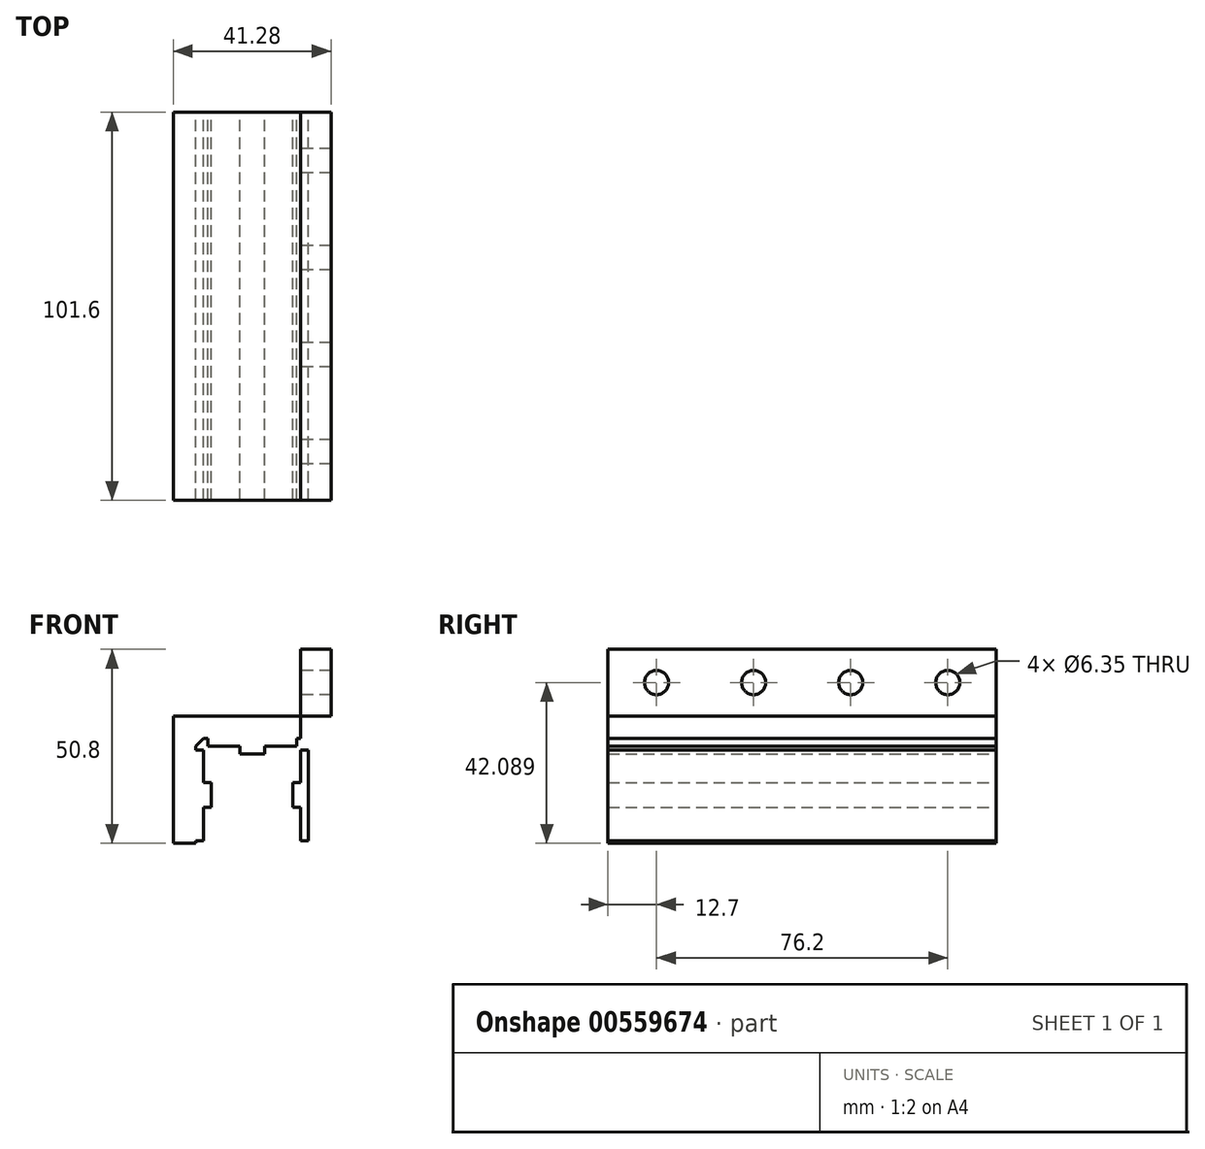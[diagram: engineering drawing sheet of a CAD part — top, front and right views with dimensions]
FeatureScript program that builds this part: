
annotation { "Feature Type Name" : "Feature", "Feature Type Description" : "" }
export const myFeature = defineFeature(function(context is Context, id is Id, definition is map)
    precondition{}
    {
        {
            var Q0;
            Q0=qCreatedBy(makeId("Front.planeOp"),FACE);
            var sketch = newSketch(context, id + "F0", { "sketchPlane" : qUnion([Q0])});
            skLineSegment(sketch, "E0.bottom", {"start": v(-20.64, 16.67) * mm, "end": v(20.64, 16.67) * mm});
            skLineSegment(sketch, "E0.top", {"start": v(-20.64, -16.67) * mm, "end": v(20.64, -16.67) * mm});
            skLineSegment(sketch, "E0.left", {"start": v(-20.64, 16.67) * mm, "end": v(-20.64, -16.67) * mm});
            skLineSegment(sketch, "E0.right", {"start": v(20.64, 16.67) * mm, "end": v(20.64, -16.67) * mm});
            skLineSegment(sketch, "E1.bottom", {"start": v(20.64, -16.67) * mm, "end": v(12.71, -16.67) * mm});
            skLineSegment(sketch, "E1.top", {"start": v(20.64, 34.13) * mm, "end": v(12.71, 34.13) * mm});
            skLineSegment(sketch, "E1.left", {"start": v(20.64, -16.67) * mm, "end": v(20.64, 34.13) * mm});
            skLineSegment(sketch, "E2.bottom", {"start": v(-12.7, -16.67) * mm, "end": v(12.7, -16.67) * mm});
            skLineSegment(sketch, "E2.top", {"start": v(-11.6, 8.73) * mm, "end": v(11.65, 8.73) * mm});
            skLineSegment(sketch, "E2.left", {"start": v(-12.7, -15.97) * mm, "end": v(-12.7, 7.78) * mm});
            skLineSegment(sketch, "E2.right", {"start": v(12.7, -15.97) * mm, "end": v(12.7, -7.2) * mm});
            skLineSegment(sketch, "E3.bottom", {"start": v(-12.7, -0.73) * mm, "end": v(-10.67, -0.73) * mm});
            skLineSegment(sketch, "E3.top", {"start": v(-12.7, -7.2) * mm, "end": v(-10.67, -7.2) * mm});
            skLineSegment(sketch, "E3.left", {"start": v(-12.7, -0.73) * mm, "end": v(-12.7, -7.2) * mm});
            skLineSegment(sketch, "E3.right", {"start": v(-10.67, -0.73) * mm, "end": v(-10.67, -7.2) * mm});
            skLineSegment(sketch, "E4.bottom", {"start": v(-3.24, 8.73) * mm, "end": v(3.24, 8.73) * mm});
            skLineSegment(sketch, "E4.top", {"start": v(-3.24, 6.7) * mm, "end": v(3.24, 6.7) * mm});
            skLineSegment(sketch, "E4.left", {"start": v(-3.24, 8.73) * mm, "end": v(-3.24, 6.7) * mm});
            skLineSegment(sketch, "E4.right", {"start": v(3.24, 8.73) * mm, "end": v(3.24, 6.7) * mm});
            skLineSegment(sketch, "E5.bottom", {"start": v(12.7, -0.73) * mm, "end": v(10.67, -0.73) * mm});
            skLineSegment(sketch, "E5.top", {"start": v(12.7, -7.2) * mm, "end": v(10.67, -7.2) * mm});
            skLineSegment(sketch, "E5.right", {"start": v(10.67, -0.73) * mm, "end": v(10.67, -7.2) * mm});
            skLineSegment(sketch, "E6", {"start": v(-10.67, -3.97) * mm, "end": v(10.67, -3.97) * mm});
            skLineSegment(sketch, "E7.top", {"start": v(-12.7, 10.76) * mm, "end": v(12.71, 10.76) * mm});
            skLineSegment(sketch, "E8.bottom", {"start": v(-12.7, -16.67) * mm, "end": v(-14.73, -16.67) * mm});
            skLineSegment(sketch, "E8.right", {"start": v(-14.73, -16.67) * mm, "end": v(-14.73, 8.73) * mm});
            skLineSegment(sketch, "E9.bottom", {"start": v(12.71, -16.67) * mm, "end": v(14.74, -16.67) * mm});
            skLineSegment(sketch, "E9.right", {"start": v(14.74, -16.67) * mm, "end": v(14.74, 8.73) * mm});
            skLineSegment(sketch, "E10", {"start": v(-14.73, 8.73) * mm, "end": v(-12.7, 10.76) * mm});
            skLineSegment(sketch, "E11", {"start": v(14.74, 8.73) * mm, "end": v(12.71, 10.76) * mm});
            skLineSegment(sketch, "E12.trimOffspring", {"start": v(12.7, -3.97) * mm, "end": v(12.71, -3.97) * mm});
            skLineSegment(sketch, "E13", {"start": v(-14.73, 7.78) * mm, "end": v(-12.7, 7.78) * mm});
            skLineSegment(sketch, "E14", {"start": v(12.71, 7.78) * mm, "end": v(14.74, 7.78) * mm});
            skLineSegment(sketch, "E15", {"start": v(11.65, 10.76) * mm, "end": v(11.65, 8.73) * mm});
            skLineSegment(sketch, "E16", {"start": v(-11.6, 10.76) * mm, "end": v(-11.6, 8.73) * mm});
            skLineSegment(sketch, "E17.trimOffspring", {"start": v(12.7, 8.73) * mm, "end": v(12.71, 8.73) * mm});
            skPoint(sketch, "E18.orphan", {"position": v(-12.7, 8.73) * mm});
            skLineSegment(sketch, "E19.trimOffspring", {"start": v(12.71, 10.76) * mm, "end": v(12.71, 34.13) * mm});
            skLineSegment(sketch, "E20", {"start": v(-14.73, -15.97) * mm, "end": v(-12.7, -15.97) * mm});
            skLineSegment(sketch, "E21.trimOffspring", {"start": v(12.7, -15.97) * mm, "end": v(14.74, -15.97) * mm});
            skLineSegment(sketch, "E22", {"start": v(12.7, -0.73) * mm, "end": v(12.71, 7.78) * mm});
            skSolve(sketch);
        }
        {
            var Q0;
            {var subQ4=sQuery(id+"F0.wireOp",EDGE,"E0.left");Q0=makeQuery(id+"F0.imprint","IMPRINT",FACE,{"disambiguationData":[TD([[makeQuery(id+"F0.imprint","IMPRINT",EDGE,{"derivedFrom":subQ4}),1.0]])]});}
            var Q1;
            {var subQ6=sQuery(id+"F0.wireOp",EDGE,"E1.bottom");Q1=makeQuery(id+"F0.imprint","IMPRINT",FACE,{"disambiguationData":[TD([[makeQuery(id+"F0.imprint","IMPRINT",EDGE,{"derivedFrom":subQ6}),-1.0]])]});}
            var Q2;
            {var subQ5=sQuery(id+"F0.wireOp",EDGE,"E1.top");Q2=makeQuery(id+"F0.imprint","IMPRINT",FACE,{"disambiguationData":[TD([[makeQuery(id+"F0.imprint","IMPRINT",EDGE,{"derivedFrom":subQ5}),1.0]])]});}
            var Q3;
            {var subQ0=sQuery(id+"F0.wireOp",EDGE,"E14");Q3=makeQuery(id+"F0.imprint","IMPRINT",FACE,{"disambiguationData":[TD([[makeQuery(id+"F0.imprint","IMPRINT",EDGE,{"derivedFrom":subQ0}),-1.0]])]});}
            var Q4;
            {var subQ3=sQuery(id+"F0.wireOp",EDGE,"E5.bottom");Q4=makeQuery(id+"F0.imprint","IMPRINT",FACE,{"disambiguationData":[TD([[makeQuery(id+"F0.imprint","IMPRINT",EDGE,{"derivedFrom":subQ3}),1.0]])]});}
            var Q5;
            {var subQ3=sQuery(id+"F0.wireOp",EDGE,"E3.bottom");Q5=makeQuery(id+"F0.imprint","IMPRINT",FACE,{"disambiguationData":[TD([[makeQuery(id+"F0.imprint","IMPRINT",EDGE,{"derivedFrom":subQ3}),-1.0]])]});}
            var Q6;
            {var subQ0=sQuery(id+"F0.wireOp",EDGE,"E13");Q6=makeQuery(id+"F0.imprint","IMPRINT",FACE,{"disambiguationData":[TD([[makeQuery(id+"F0.imprint","IMPRINT",EDGE,{"derivedFrom":subQ0}),-1.0]])]});}
            var Q7;
            Q7=makeQuery(id+"F0.imprint","IMPRINT",FACE,{"disambiguationData":[TD([[makeQuery(id+"F0.imprint","IMPRINT",EDGE,{"derivedFrom":sQuery(id+"F0.wireOp",EDGE,"E4.top")}),1.0]])]});
            var Q8;
            {var subQ0=sQuery(id+"F0.wireOp",EDGE,"E15");Q8=makeQuery(id+"F0.imprint","IMPRINT",FACE,{"disambiguationData":[TD([[makeQuery(id+"F0.imprint","IMPRINT",EDGE,{"derivedFrom":subQ0}),-1.0]])]});}
            extrude(context, id + "F1", {"entities" : qUnion([Q0, Q1, Q2, Q3, Q4, Q5, Q6, Q7, Q8]), "depth" : 101.6 * mm, "offsetDistance" : 25.4 * mm});
        }
        {
            var Q0;
            Q0=makeQuery(id+"F1.opExtrude","SWEPT_FACE",FACE,{"disambiguationData":[OSD([sQuery(id+"F0.wireOp",EDGE,"E19.trimOffspring")])]});
            var sketch = newSketch(context, id + "F2", { "sketchPlane" : qUnion([Q0])});
            skCircle(sketch, "E23", {"center": v(88.9, 25.42) * mm, "radius": 3.18 * mm});
            skCircle(sketch, "E24", {"center": v(63.5, 25.42) * mm, "radius": 3.18 * mm});
            skCircle(sketch, "E25", {"center": v(38.1, 25.42) * mm, "radius": 3.18 * mm});
            skCircle(sketch, "E26", {"center": v(12.7, 25.42) * mm, "radius": 3.18 * mm});
            skSolve(sketch);
        }
        {
            var Q0;
            Q0=makeQuery(id+"F2.imprint","IMPRINT",FACE,{"disambiguationData":[TD([[makeQuery(id+"F2.imprint","IMPRINT",EDGE,{"derivedFrom":sQuery(id+"F2.wireOp",EDGE,"E26")}),1.0]])]});
            var Q1;
            Q1=makeQuery(id+"F2.imprint","IMPRINT",FACE,{"disambiguationData":[TD([[makeQuery(id+"F2.imprint","IMPRINT",EDGE,{"derivedFrom":sQuery(id+"F2.wireOp",EDGE,"E25")}),1.0]])]});
            var Q2;
            Q2=makeQuery(id+"F2.imprint","IMPRINT",FACE,{"disambiguationData":[TD([[makeQuery(id+"F2.imprint","IMPRINT",EDGE,{"derivedFrom":sQuery(id+"F2.wireOp",EDGE,"E24")}),1.0]])]});
            var Q3;
            Q3=makeQuery(id+"F2.imprint","IMPRINT",FACE,{"disambiguationData":[TD([[makeQuery(id+"F2.imprint","IMPRINT",EDGE,{"derivedFrom":sQuery(id+"F2.wireOp",EDGE,"E23")}),1.0]])]});
            extrude(context, id + "F3", {"entities" : qUnion([Q0, Q1, Q2, Q3]), "operationType" : NewBodyOperationType.REMOVE, "endBound" : BoundingType.THROUGH_ALL, "oppositeDirection" : true, "depth" : 25.4 * mm, "offsetDistance" : 25.4 * mm});
        }
    });
